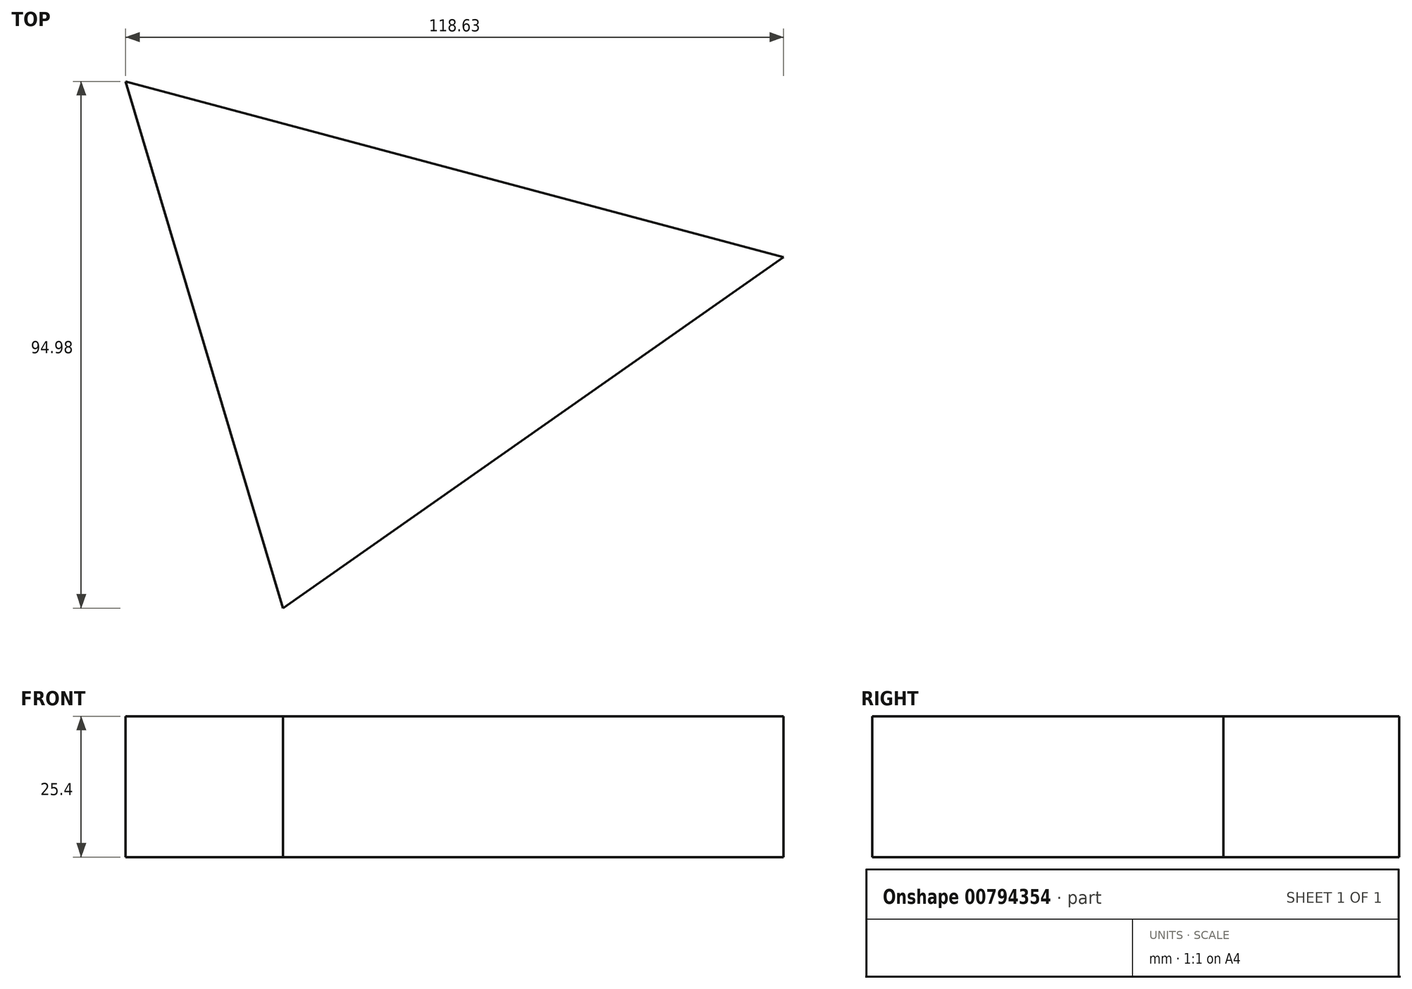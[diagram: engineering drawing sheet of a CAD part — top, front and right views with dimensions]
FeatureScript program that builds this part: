
annotation { "Feature Type Name" : "Feature", "Feature Type Description" : "" }
export const myFeature = defineFeature(function(context is Context, id is Id, definition is map)
    precondition{}
    {
        {
            var Q0;
            Q0=qCreatedBy(makeId("Top.planeOp"),FACE);
            var sketch = newSketch(context, id + "F0", { "sketchPlane" : qUnion([Q0])});
            skLineSegment(sketch, "E0", {"start": v(0, 9) * mm, "end": v(-90.24, -54.27) * mm});
            skLineSegment(sketch, "E1", {"start": v(-90.24, -54.27) * mm, "end": v(-118.63, 40.7) * mm});
            skLineSegment(sketch, "E2", {"start": v(-118.63, 40.7) * mm, "end": v(0, 9) * mm});
            skSolve(sketch);
        }
        {
            var Q0;
            Q0=makeQuery(id+"F0.imprint","IMPRINT",FACE,{"disambiguationData":[TD([[makeQuery(id+"F0.imprint","IMPRINT",EDGE,{"derivedFrom":sQuery(id+"F0.wireOp",EDGE,"E0")}),-1.0]])]});
            extrude(context, id + "F1", {"entities" : qUnion([Q0]), "depth" : 25.4 * mm, "offsetDistance" : 25.4 * mm});
        }
    });
